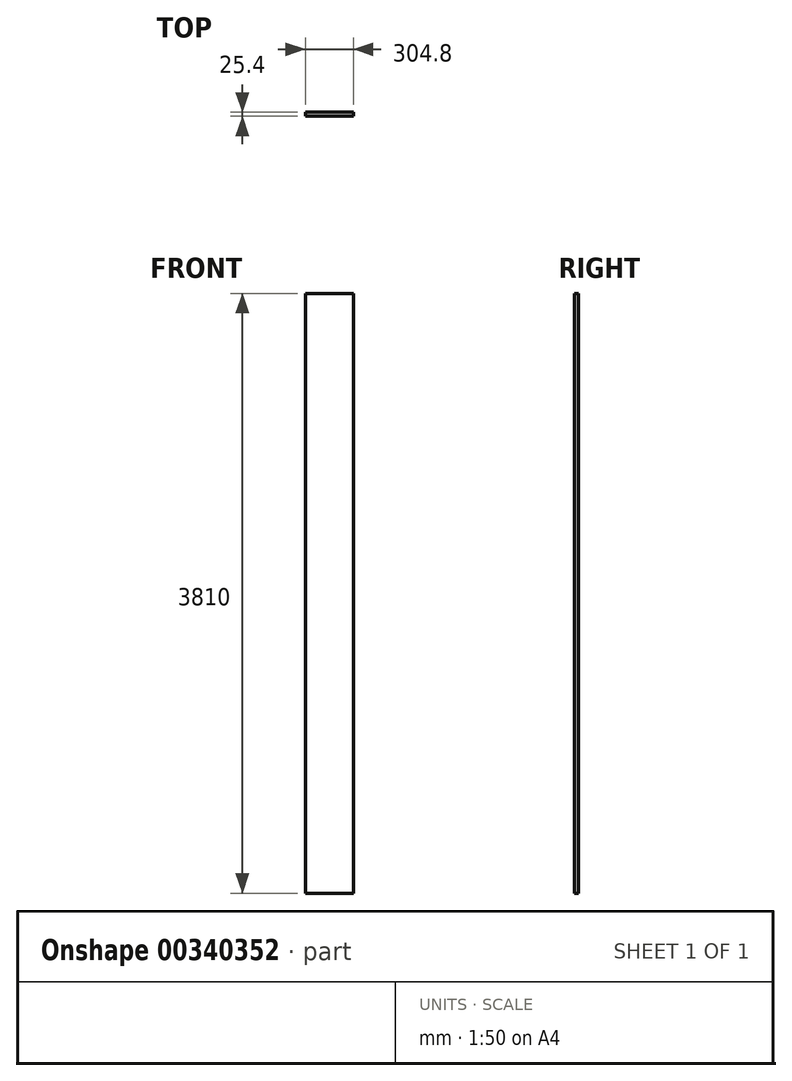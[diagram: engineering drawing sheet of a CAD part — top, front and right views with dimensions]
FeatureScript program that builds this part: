
annotation { "Feature Type Name" : "Feature", "Feature Type Description" : "" }
export const myFeature = defineFeature(function(context is Context, id is Id, definition is map)
    precondition{}
    {
        {
            var Q0;
            Q0=qCreatedBy(makeId("Front.planeOp"),FACE);
            var sketch = newSketch(context, id + "F0", { "sketchPlane" : qUnion([Q0])});
            skLineSegment(sketch, "E0.bottom", {"start": v(-155.69, 2418.24) * mm, "end": v(149.11, 2418.24) * mm});
            skLineSegment(sketch, "E0.top", {"start": v(-155.69, -1391.76) * mm, "end": v(149.11, -1391.76) * mm});
            skLineSegment(sketch, "E0.left", {"start": v(-155.69, 2418.24) * mm, "end": v(-155.69, -1391.76) * mm});
            skLineSegment(sketch, "E0.right", {"start": v(149.11, 2418.24) * mm, "end": v(149.11, -1391.76) * mm});
            skSolve(sketch);
        }
        {
            var Q0;
            Q0 = qSketchRegion(id + "F0", true);
            extrude(context, id + "F1", {"entities" : qUnion([Q0]), "depth" : 25.4 * mm});
        }
    });
